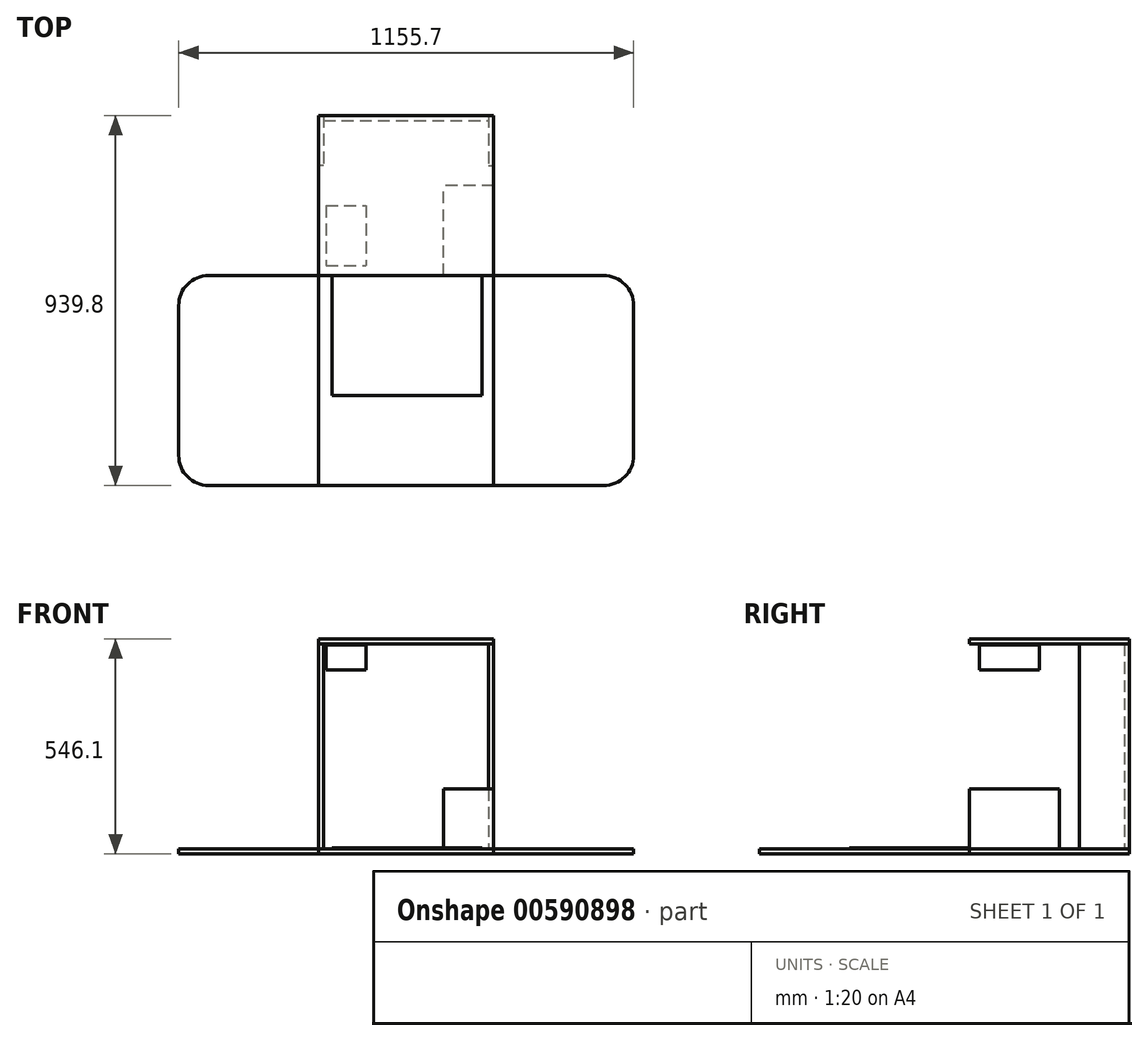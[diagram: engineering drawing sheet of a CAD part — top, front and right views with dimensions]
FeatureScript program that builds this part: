
annotation { "Feature Type Name" : "Feature", "Feature Type Description" : "" }
export const myFeature = defineFeature(function(context is Context, id is Id, definition is map)
    precondition{}
    {
        {
            var Q0;
            Q0=qCreatedBy(makeId("Top.planeOp"),FACE);
            var sketch = newSketch(context, id + "F0", { "sketchPlane" : qUnion([Q0])});
            skCircle(sketch, "E0", {"center": v(0, 0) * mm, "radius": 609.6 * mm, "construction": true});
            skLineSegment(sketch, "E1.bottom", {"start": v(-222.25, -609.6) * mm, "end": v(222.25, -609.6) * mm});
            skLineSegment(sketch, "E1.top", {"start": v(-222.25, -76.2) * mm, "end": v(222.25, -76.2) * mm});
            skLineSegment(sketch, "E1.left", {"start": v(-222.25, -609.6) * mm, "end": v(-222.25, -76.2) * mm});
            skLineSegment(sketch, "E1.right", {"start": v(222.25, -609.6) * mm, "end": v(222.25, -76.2) * mm});
            skPoint(sketch, "E1.middle", {"position": v(0, -342.9) * mm});
            skLineSegment(sketch, "E2.bottom", {"start": v(-222.25, -76.2) * mm, "end": v(-577.85, -76.2) * mm});
            skLineSegment(sketch, "E2.top", {"start": v(-222.25, -609.6) * mm, "end": v(-577.85, -609.6) * mm});
            skLineSegment(sketch, "E2.left", {"start": v(-222.25, -76.2) * mm, "end": v(-222.25, -609.6) * mm});
            skLineSegment(sketch, "E2.right", {"start": v(-577.85, -76.2) * mm, "end": v(-577.85, -609.6) * mm});
            skLineSegment(sketch, "E3.bottom", {"start": v(222.25, -76.2) * mm, "end": v(577.85, -76.2) * mm});
            skLineSegment(sketch, "E3.top", {"start": v(222.25, -609.6) * mm, "end": v(577.85, -609.6) * mm});
            skLineSegment(sketch, "E3.left", {"start": v(222.25, -76.2) * mm, "end": v(222.25, -609.6) * mm});
            skLineSegment(sketch, "E3.right", {"start": v(577.85, -76.2) * mm, "end": v(577.85, -609.6) * mm});
            skLineSegment(sketch, "E4.bottom", {"start": v(-209.55, 330.2) * mm, "end": v(209.55, 330.2) * mm});
            skLineSegment(sketch, "E4.top", {"start": v(-209.55, 203.2) * mm, "end": v(209.55, 203.2) * mm});
            skLineSegment(sketch, "E4.left", {"start": v(-209.55, 330.2) * mm, "end": v(-209.55, 203.2) * mm});
            skLineSegment(sketch, "E4.right", {"start": v(209.55, 330.2) * mm, "end": v(209.55, 203.2) * mm});
            skLineSegment(sketch, "E5.bottom", {"start": v(-209.55, 330.2) * mm, "end": v(-222.25, 330.2) * mm});
            skLineSegment(sketch, "E5.top", {"start": v(-209.55, 203.2) * mm, "end": v(-222.25, 203.2) * mm});
            skLineSegment(sketch, "E5.right", {"start": v(-222.25, 330.2) * mm, "end": v(-222.25, 203.2) * mm});
            skLineSegment(sketch, "E6.bottom", {"start": v(209.55, 330.2) * mm, "end": v(222.25, 330.2) * mm});
            skLineSegment(sketch, "E6.top", {"start": v(209.55, 203.2) * mm, "end": v(222.25, 203.2) * mm});
            skLineSegment(sketch, "E6.right", {"start": v(222.25, 330.2) * mm, "end": v(222.25, 203.2) * mm});
            skLineSegment(sketch, "E7", {"start": v(0, 203.2) * mm, "end": v(0, 288.07) * mm, "construction": true});
            skLineSegment(sketch, "E8", {"start": v(-209.55, 203.2) * mm, "end": v(-209.55, -76.2) * mm});
            skLineSegment(sketch, "E9", {"start": v(209.55, 203.2) * mm, "end": v(209.55, -76.2) * mm});
            skLineSegment(sketch, "E10", {"start": v(-222.25, -76.2) * mm, "end": v(-222.25, 203.2) * mm});
            skLineSegment(sketch, "E11", {"start": v(222.25, -76.2) * mm, "end": v(222.25, 203.2) * mm});
            skSolve(sketch);
        }
        {
            var Q0;
            Q0=makeQuery(id+"F0.imprint","IMPRINT",FACE,{"disambiguationData":[TD([[makeQuery(id+"F0.imprint","IMPRINT",EDGE,{"derivedFrom":sQuery(id+"F0.wireOp",EDGE,"E2.bottom")}),1.0]])]});
            extrude(context, id + "F1", {"entities" : qUnion([Q0]), "depth" : 12.7 * mm, "offsetDistance" : 25.4 * mm});
        }
        {
            var Q0;
            Q0=makeQuery(id+"F0.imprint","IMPRINT",FACE,{"disambiguationData":[TD([[makeQuery(id+"F0.imprint","IMPRINT",EDGE,{"derivedFrom":sQuery(id+"F0.wireOp",EDGE,"E1.bottom")}),1.0]])]});
            extrude(context, id + "F2", {"entities" : qUnion([Q0]), "depth" : 12.7 * mm, "offsetDistance" : 25.4 * mm});
        }
        {
            var Q0;
            Q0=makeQuery(id+"F0.imprint","IMPRINT",FACE,{"disambiguationData":[TD([[makeQuery(id+"F0.imprint","IMPRINT",EDGE,{"derivedFrom":sQuery(id+"F0.wireOp",EDGE,"E3.bottom")}),-1.0]])]});
            extrude(context, id + "F3", {"entities" : qUnion([Q0]), "depth" : 12.7 * mm, "offsetDistance" : 25.4 * mm});
        }
        {
            var Q0;
            Q0=makeQuery(id+"F0.imprint","IMPRINT",FACE,{"disambiguationData":[TD([[makeQuery(id+"F0.imprint","IMPRINT",EDGE,{"derivedFrom":sQuery(id+"F0.wireOp",EDGE,"E4.top")}),-1.0]])]});
            var Q1;
            Q1=makeQuery(id+"F0.imprint","IMPRINT",FACE,{"disambiguationData":[TD([[makeQuery(id+"F0.imprint","IMPRINT",EDGE,{"derivedFrom":sQuery(id+"F0.wireOp",EDGE,"E5.top")}),1.0]])]});
            var Q2;
            Q2=makeQuery(id+"F0.imprint","IMPRINT",FACE,{"disambiguationData":[TD([[makeQuery(id+"F0.imprint","IMPRINT",EDGE,{"derivedFrom":sQuery(id+"F0.wireOp",EDGE,"E6.top")}),-1.0]])]});
            var Q3;
            Q3=makeQuery(id+"F0.imprint","IMPRINT",FACE,{"disambiguationData":[TD([[makeQuery(id+"F0.imprint","IMPRINT",EDGE,{"derivedFrom":sQuery(id+"F0.wireOp",EDGE,"E4.bottom")}),-1.0]])]});
            var Q4;
            Q4=makeQuery(id+"F0.imprint","IMPRINT",FACE,{"disambiguationData":[TD([[makeQuery(id+"F0.imprint","IMPRINT",EDGE,{"derivedFrom":sQuery(id+"F0.wireOp",EDGE,"E6.bottom")}),-1.0]])]});
            var Q5;
            Q5=makeQuery(id+"F0.imprint","IMPRINT",FACE,{"disambiguationData":[TD([[makeQuery(id+"F0.imprint","IMPRINT",EDGE,{"derivedFrom":sQuery(id+"F0.wireOp",EDGE,"E5.bottom")}),1.0]])]});
            extrude(context, id + "F4", {"entities" : qUnion([Q0, Q1, Q2, Q3, Q4, Q5]), "depth" : 12.7 * mm, "offsetDistance" : 25.4 * mm});
        }
        {
            var Q0;
            Q0=makeQuery(id+"F4.opExtrude","CAP_FACE",FACE,{"disambiguationData":[OSD([sQuery(id+"F0.wireOp",EDGE,"E1.top"),sQuery(id+"F0.wireOp",EDGE,"E4.bottom"),sQuery(id+"F0.wireOp",EDGE,"E5.bottom"),sQuery(id+"F0.wireOp",EDGE,"E5.right"),sQuery(id+"F0.wireOp",EDGE,"E6.bottom"),sQuery(id+"F0.wireOp",EDGE,"E6.right"),sQuery(id+"F0.wireOp",EDGE,"E10"),sQuery(id+"F0.wireOp",EDGE,"E11")])],"isStart":false});
            var sketch = newSketch(context, id + "F5", { "sketchPlane" : qUnion([Q0])});
            skLineSegment(sketch, "E12.0", {"start": v(-209.55, 330.2) * mm, "end": v(209.55, 330.2) * mm});
            skLineSegment(sketch, "E13.0", {"start": v(-209.55, 330.2) * mm, "end": v(-209.55, 203.2) * mm});
            skLineSegment(sketch, "E14.0", {"start": v(-209.55, 203.2) * mm, "end": v(-222.25, 203.2) * mm});
            skLineSegment(sketch, "E15.0", {"start": v(-222.25, 330.2) * mm, "end": v(-222.25, 203.2) * mm});
            skLineSegment(sketch, "E16.0", {"start": v(-209.55, 330.2) * mm, "end": v(-222.25, 330.2) * mm});
            skLineSegment(sketch, "E17.0", {"start": v(222.25, -76.2) * mm, "end": v(222.25, 330.2) * mm});
            skLineSegment(sketch, "E18.0", {"start": v(209.55, 330.2) * mm, "end": v(222.25, 330.2) * mm});
            skLineSegment(sketch, "E19.0", {"start": v(209.55, 330.2) * mm, "end": v(209.55, 203.2) * mm});
            skLineSegment(sketch, "E20.0", {"start": v(209.55, 203.2) * mm, "end": v(222.25, 203.2) * mm});
            skLineSegment(sketch, "E21", {"start": v(-209.55, 317.5) * mm, "end": v(209.55, 317.5) * mm});
            skSolve(sketch);
        }
        {
            var Q0;
            Q0=makeQuery(id+"F4.opExtrude","SWEPT_BODY",BODY,{"disambiguationData":[OSD([sQuery(id+"F0.wireOp",EDGE,"E1.top"),sQuery(id+"F0.wireOp",EDGE,"E4.bottom"),sQuery(id+"F0.wireOp",EDGE,"E5.bottom"),sQuery(id+"F0.wireOp",EDGE,"E5.right"),sQuery(id+"F0.wireOp",EDGE,"E6.bottom"),sQuery(id+"F0.wireOp",EDGE,"E6.right"),sQuery(id+"F0.wireOp",EDGE,"E10"),sQuery(id+"F0.wireOp",EDGE,"E11")])]});
            transform(context, id + "F6", {"entities" : qUnion([Q0]), "transformType" : TransformType.TRANSLATION_3D, "dx" : 0 * mm, "dy" : 0 * mm, "dz" : 533.4 * mm, "makeCopy" : true});
        }
        {
            var Q0;
            {var subQ0=sQuery(id+"F5.wireOp",EDGE,"E14.0");Q0=makeQuery(id+"F5.imprint","IMPRINT",FACE,{"disambiguationData":[TD([[makeQuery(id+"F5.imprint","IMPRINT",EDGE,{"derivedFrom":subQ0}),-1.0]])]});}
            var Q1;
            {var subQ3=sQuery(id+"F5.wireOp",EDGE,"E18.0");Q1=makeQuery(id+"F5.imprint","IMPRINT",FACE,{"disambiguationData":[TD([[makeQuery(id+"F5.imprint","IMPRINT",EDGE,{"derivedFrom":subQ3}),-1.0]])]});}
            var Q2;
            Q2=makeQuery(id+"F6.opPattern","COPY",FACE,{"derivedFrom":makeQuery(id+"F4.opExtrude","CAP_FACE",FACE,{"disambiguationData":[OSD([sQuery(id+"F0.wireOp",EDGE,"E1.top"),sQuery(id+"F0.wireOp",EDGE,"E4.bottom"),sQuery(id+"F0.wireOp",EDGE,"E5.bottom"),sQuery(id+"F0.wireOp",EDGE,"E5.right"),sQuery(id+"F0.wireOp",EDGE,"E6.bottom"),sQuery(id+"F0.wireOp",EDGE,"E6.right"),sQuery(id+"F0.wireOp",EDGE,"E10"),sQuery(id+"F0.wireOp",EDGE,"E11")])],"isStart":true}),"instanceName":"1"});
            extrude(context, id + "F7", {"entities" : qUnion([Q0, Q1]), "endBound" : BoundingType.UP_TO_SURFACE, "depth" : 25.4 * mm, "endBoundEntityFace" : qUnion([Q2]), "offsetDistance" : 25.4 * mm});
        }
        {
            var Q0;
            {var subQ0=sQuery(id+"F5.wireOp",EDGE,"E12.0");Q0=makeQuery(id+"F5.imprint","IMPRINT",FACE,{"disambiguationData":[TD([[makeQuery(id+"F5.imprint","IMPRINT",EDGE,{"derivedFrom":subQ0}),-1.0]])]});}
            var Q1;
            Q1=makeQuery(id+"F6.opPattern","COPY",FACE,{"derivedFrom":makeQuery(id+"F4.opExtrude","CAP_FACE",FACE,{"disambiguationData":[OSD([sQuery(id+"F0.wireOp",EDGE,"E1.top"),sQuery(id+"F0.wireOp",EDGE,"E4.bottom"),sQuery(id+"F0.wireOp",EDGE,"E5.bottom"),sQuery(id+"F0.wireOp",EDGE,"E5.right"),sQuery(id+"F0.wireOp",EDGE,"E6.bottom"),sQuery(id+"F0.wireOp",EDGE,"E6.right"),sQuery(id+"F0.wireOp",EDGE,"E10"),sQuery(id+"F0.wireOp",EDGE,"E11")])],"isStart":true}),"instanceName":"1"});
            extrude(context, id + "F8", {"entities" : qUnion([Q0]), "endBound" : BoundingType.UP_TO_SURFACE, "depth" : 25.4 * mm, "endBoundEntityFace" : qUnion([Q1]), "offsetDistance" : 25.4 * mm});
        }
        {
            var Q0;
            Q0=makeQuery(id+"F1.opExtrude","SWEPT_EDGE",EDGE,{"disambiguationData":[OSD([sQuery(id+"F0.wireOp",EDGE,"E2.top"),sQuery(id+"F0.wireOp",EDGE,"E2.right")])]});
            var Q1;
            Q1=makeQuery(id+"F3.opExtrude","SWEPT_EDGE",EDGE,{"disambiguationData":[OSD([sQuery(id+"F0.wireOp",EDGE,"E3.top"),sQuery(id+"F0.wireOp",EDGE,"E3.right")])]});
            var Q2;
            Q2=makeQuery(id+"F1.opExtrude","SWEPT_EDGE",EDGE,{"disambiguationData":[OSD([sQuery(id+"F0.wireOp",EDGE,"E2.bottom"),sQuery(id+"F0.wireOp",EDGE,"E2.right")])]});
            var Q3;
            Q3=makeQuery(id+"F3.opExtrude","SWEPT_EDGE",EDGE,{"disambiguationData":[OSD([sQuery(id+"F0.wireOp",EDGE,"E3.bottom"),sQuery(id+"F0.wireOp",EDGE,"E3.right")])]});
            fillet(context, id + "F9", {"entities" : qUnion([Q0, Q1, Q2, Q3]), "radius" : 76.2 * mm, "tangentPropagation" : true, "allowEdgeOverflow" : false});
        }
        {
            var Q0;
            Q0=makeQuery(id+"F2.opExtrude","CAP_FACE",FACE,{"disambiguationData":[OSD([sQuery(id+"F0.wireOp",EDGE,"E1.bottom"),sQuery(id+"F0.wireOp",EDGE,"E1.top"),sQuery(id+"F0.wireOp",EDGE,"E2.left"),sQuery(id+"F0.wireOp",EDGE,"E3.left")])],"isStart":false});
            var sketch = newSketch(context, id + "F10", { "sketchPlane" : qUnion([Q0])});
            skLineSegment(sketch, "E22.bottom", {"start": v(222.25, -76.2) * mm, "end": v(95.25, -76.2) * mm});
            skLineSegment(sketch, "E22.top", {"start": v(222.25, 152.4) * mm, "end": v(95.25, 152.4) * mm});
            skLineSegment(sketch, "E22.left", {"start": v(222.25, -76.2) * mm, "end": v(222.25, 152.4) * mm});
            skLineSegment(sketch, "E22.right", {"start": v(95.25, -76.2) * mm, "end": v(95.25, 152.4) * mm});
            skLineSegment(sketch, "E23.bottom", {"start": v(-203.2, 177.8) * mm, "end": v(-101.6, 177.8) * mm});
            skLineSegment(sketch, "E23.top", {"start": v(-203.2, 25.4) * mm, "end": v(-101.6, 25.4) * mm});
            skLineSegment(sketch, "E23.left", {"start": v(-203.2, 177.8) * mm, "end": v(-203.2, 25.4) * mm});
            skLineSegment(sketch, "E23.right", {"start": v(-101.6, 177.8) * mm, "end": v(-101.6, 25.4) * mm});
            skLineSegment(sketch, "E24.bottom", {"start": v(-188.25, -76.2) * mm, "end": v(192.75, -76.2) * mm});
            skLineSegment(sketch, "E24.top", {"start": v(-188.25, -381) * mm, "end": v(192.75, -381) * mm});
            skLineSegment(sketch, "E24.left", {"start": v(-188.25, -76.2) * mm, "end": v(-188.25, -381) * mm});
            skLineSegment(sketch, "E24.right", {"start": v(192.75, -76.2) * mm, "end": v(192.75, -381) * mm});
            skSolve(sketch);
        }
        {
            var Q0;
            Q0=makeQuery(id+"F10.imprint","IMPRINT",FACE,{"disambiguationData":[TD([[makeQuery(id+"F10.imprint","IMPRINT",EDGE,{"derivedFrom":sQuery(id+"F10.wireOp",EDGE,"E24.top")}),1.0]])]});
            extrude(context, id + "F11", {"entities" : qUnion([Q0]), "depth" : 2.54 * mm, "offsetDistance" : 25.4 * mm});
        }
        {
            var Q0;
            {var subQ1=sQuery(id+"F10.wireOp",EDGE,"E22.bottom");Q0=makeQuery(id+"F10.imprint","IMPRINT",FACE,{"disambiguationData":[TD([[makeQuery(id+"F10.imprint","IMPRINT",EDGE,{"derivedFrom":subQ1}),1.0]])]});}
            extrude(context, id + "F12", {"entities" : qUnion([Q0]), "depth" : 152.4 * mm, "offsetDistance" : 25.4 * mm});
        }
        {
            var Q0;
            Q0=makeQuery(id+"F10.imprint","IMPRINT",FACE,{"disambiguationData":[TD([[makeQuery(id+"F10.imprint","IMPRINT",EDGE,{"derivedFrom":sQuery(id+"F10.wireOp",EDGE,"E23.top")}),1.0]])]});
            extrude(context, id + "F13", {"entities" : qUnion([Q0]), "depth" : 63.5 * mm, "offsetDistance" : 25.4 * mm});
        }
        {
            var Q0;
            Q0=makeQuery(id+"F13.opExtrude","SWEPT_BODY",BODY,{"disambiguationData":[OSD([sQuery(id+"F10.wireOp",EDGE,"E23.bottom"),sQuery(id+"F10.wireOp",EDGE,"E23.top"),sQuery(id+"F10.wireOp",EDGE,"E23.left"),sQuery(id+"F10.wireOp",EDGE,"E23.right")])]});
            transform(context, id + "F14", {"entities" : qUnion([Q0]), "transformType" : TransformType.TRANSLATION_3D, "dx" : 0 * mm, "dy" : -76.2 * mm, "dz" : 454.66 * mm, "makeCopy" : false});
        }
    });
